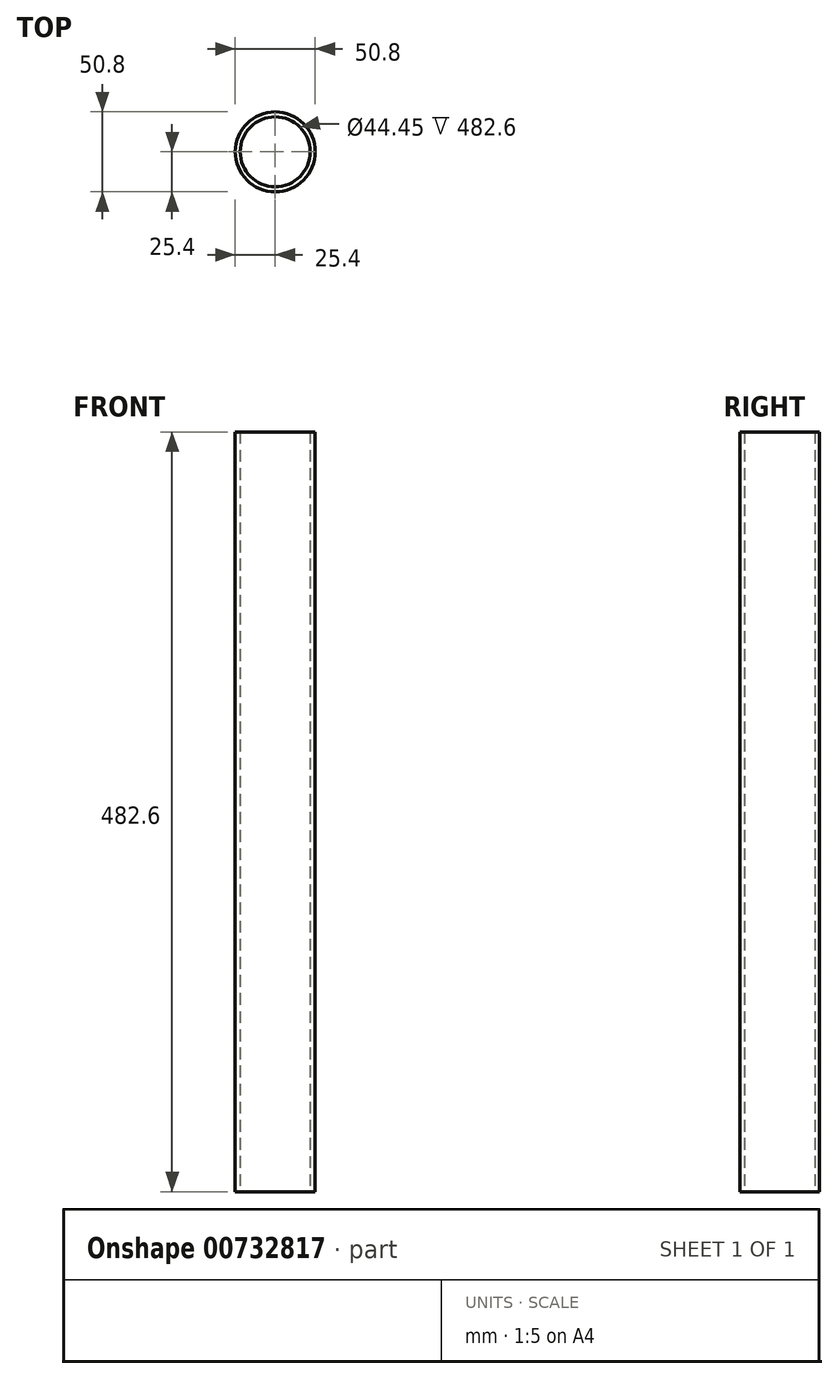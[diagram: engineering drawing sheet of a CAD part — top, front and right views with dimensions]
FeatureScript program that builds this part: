
annotation { "Feature Type Name" : "Feature", "Feature Type Description" : "" }
export const myFeature = defineFeature(function(context is Context, id is Id, definition is map)
    precondition{}
    {
        {
            var Q0;
            Q0=qCreatedBy(makeId("Top.planeOp"),FACE);
            var sketch = newSketch(context, id + "F0", { "sketchPlane" : qUnion([Q0])});
            skCircle(sketch, "E0", {"center": v(0, 0) * mm, "radius": 25.4 * mm});
            skCircle(sketch, "E1.0", {"center": v(0, 0) * mm, "radius": 22.23 * mm});
            skSolve(sketch);
        }
        {
            var Q0;
            Q0 = qSketchRegion(id + "F0", true);
            extrude(context, id + "F1", {"entities" : qUnion([Q0]), "depth" : 482.6 * mm, "offsetDistance" : 25.4 * mm});
        }
    });
